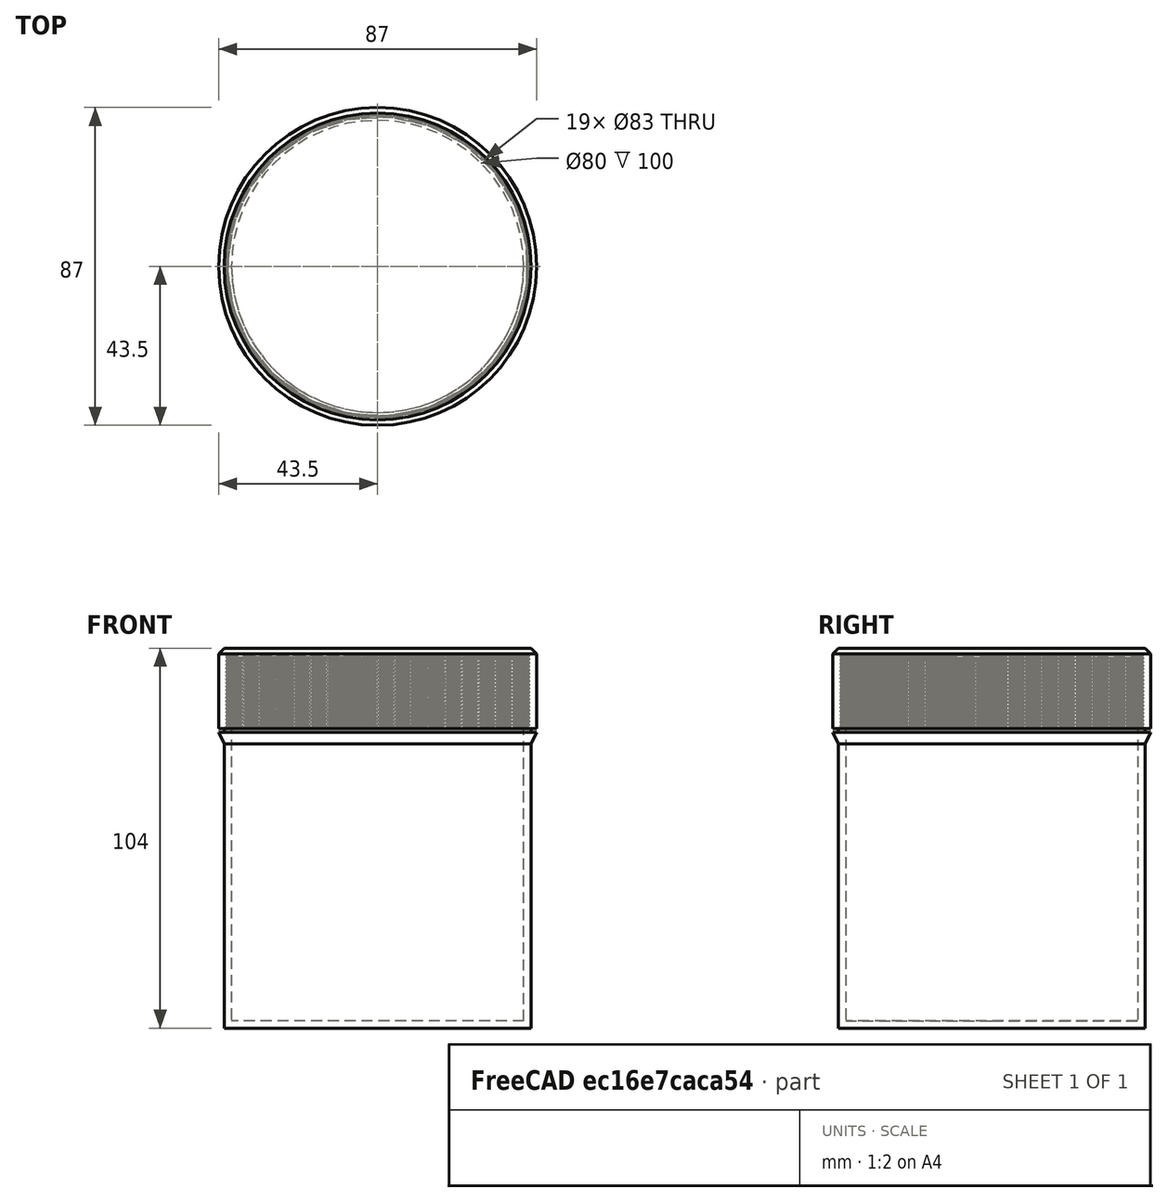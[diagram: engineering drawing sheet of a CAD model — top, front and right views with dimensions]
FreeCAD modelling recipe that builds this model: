
FCSTD DOCUMENT  (FreeCAD 1.0R38641 +678 (Git))
Label: Parametric Screw Top Container
License: All rights reserved
LicenseURL: http://en.wikipedia.org/wiki/All_rights_reserved
objects: Sketcher::SketchObject×9, PartDesign::Pad×2, PartDesign::AdditiveHelix×2, PartDesign::Groove×2, PartDesign::Revolution×2, PartDesign::Body×2, Spreadsheet::Sheet×1, PartDesign::Pocket×1
note: 47 computed .brp shape members not serialized (recipe doc carries the construction recipe); baked Part::Feature solids carry a one-line shape summary decoded from their .brp

FEATURE [Spreadsheet::Sheet] Spreadsheet  label="Parameters"
  cells = A2='Property; B2='Value; D2='Calculated Properties; G2='Some Presets; H2='Stores...; A3='Inner Diameter; B3(innerdiameter)==80 mm; D3='Thread Pitch; E3(threadpitch)==ceil(B5 / 2); G3='19.5 x 77.5; H3='50 US Pennies (1 Roll, $0.50); A4='Inner Height; B4(innerheight)==100 mm; D4='Thread Height; E4(threadheight)==B4 * 0.25 > 20 ? 20 mm : B4 * 0.25; G4='21.75 x 74; H4='40 US Nickels (1 Roll, $2); A5='Wall Thickness; B5(wallthickness)==2 mm; D5='Total Height; E5(totalheight)==B4 + B6; G5='18 x 70; H5='50 US Dimes (1 Roll, $5); A6='Floor Thickness; B6(floorthickness)==2 mm; G6='24.5 x 74; H6='40 US Quarters (1 Roll, $10); A7='Cap Thickness; B7(capthickness)==2 mm; G7='29.5 x 40; H7='Complete KLR650 Valve Shim Set; G8='18.5 x 65.1; H8='One 18650 Cell (Natch); G9='10.5 x 45; H9='One AAA Cell; G10='14.5 x 50.5; H10='One AA Cell; G11='26 x 50; H11='One C Cell; G12='33.5 x 60.25; H12='One D Cell
FEATURE [Sketcher::SketchObject] Sketch  label="Floor Sketch"
  ArcFitTolerance = 0
  AttachmentSupport = -> [XY_Plane]
  FullyConstrained = true
  MakeInternals = false
  MapMode = 5
  expr: Constraints[1] = Spreadsheet.innerdiameter + Spreadsheet.wallthickness * 2
  sketch-geometry (1):
    g0: Circle CenterX=0 CenterY=0 CenterZ=0 NormalX=0 NormalY=0 NormalZ=1 AngleXU=0 Radius=42
  constraints (2):
    c: Coincident(g0,g-1)
    c: Diameter(g0) = 84
FEATURE [Sketcher::SketchObject] Sketch001  label="Walls Sketch"
  ArcFitTolerance = 0
  AttachmentOffset = pos=(0,0,2) rot=(0,0,1;0rad)
  AttachmentSupport = -> [XY_Plane]
  FullyConstrained = true
  MakeInternals = false
  MapMode = 5
  Placement = pos=(0,0,2) rot=(0,0,1;0rad)
  expr: .AttachmentOffset.Base.z = Spreadsheet.floorthickness
  expr: Constraints[1] = Spreadsheet.innerdiameter
  expr: Constraints[3] = Spreadsheet.innerdiameter + Spreadsheet.wallthickness * 2
  sketch-geometry (2):
    g0: Circle CenterX=0 CenterY=0 CenterZ=0 NormalX=0 NormalY=0 NormalZ=1 AngleXU=0 Radius=40
    g1: Circle CenterX=0 CenterY=0 CenterZ=0 NormalX=0 NormalY=0 NormalZ=1 AngleXU=0 Radius=42
  constraints (4):
    c: Coincident(g0,g-1)
    c: Diameter(g0) = 80
    c: Coincident(g1,g0)
    c: Diameter(g1) = 84
FEATURE [PartDesign::Pad] Pad  label="Floor Pad"
  Direction = (0,0,1)
  Length = 2
  Length2 = 10
  Profile = -> Sketch
  ReferenceAxis = -> Sketch [N_Axis]
  Suppressed = false
  Type = 0
  expr: Length = Spreadsheet.floorthickness
FEATURE [PartDesign::Pad] Pad001  label="Walls Pad"
  BaseFeature = -> Pad
  Direction = (0,0,1)
  Length = 100
  Length2 = 10
  Profile = -> Sketch001
  ReferenceAxis = -> Sketch001 [N_Axis]
  Suppressed = false
  Type = 0
  expr: Length = Spreadsheet.innerheight
FEATURE [Sketcher::SketchObject] Sketch002  label="Thinner Sketch"
  ArcFitTolerance = 0
  AttachmentOffset = pos=(0,0,102) rot=(0,0,1;0rad)
  AttachmentSupport = -> [XY_Plane]
  FullyConstrained = true
  MakeInternals = false
  MapMode = 5
  Placement = pos=(0,0,102) rot=(0,0,1;0rad)
  expr: .AttachmentOffset.Base.z = Spreadsheet.totalheight
  expr: Constraints[2] = Spreadsheet.innerdiameter + Spreadsheet.wallthickness * 2
  expr: Constraints[3] = Spreadsheet.innerdiameter + Spreadsheet.wallthickness
  sketch-geometry (2):
    g0: Circle CenterX=0 CenterY=0 CenterZ=0 NormalX=0 NormalY=0 NormalZ=1 AngleXU=0 Radius=42
    g1: Circle CenterX=0 CenterY=0 CenterZ=0 NormalX=0 NormalY=0 NormalZ=1 AngleXU=0 Radius=41
  constraints (4):
    c: Coincident(g0,g-1)
    c: Coincident(g1,g0)
    c: Diameter(g0) = 84
    c: Diameter(g1) = 82
FEATURE [PartDesign::Pocket] Pocket  label="Thinner Cut"
  BaseFeature = -> Pad001
  Direction = (0,0,-1)
  Length = 20
  Length2 = 5
  Profile = -> Sketch002
  ReferenceAxis = -> Sketch002 [N_Axis]
  Suppressed = false
  Type = 0
  expr: Length = Spreadsheet.threadheight
FEATURE [Sketcher::SketchObject] Sketch003  label="Male Thread Tooth Sketch"
  ArcFitTolerance = 0
  AttachmentSupport = -> [XZ_Plane]
  FullyConstrained = true
  MakeInternals = false
  MapMode = 5
  Placement = pos=(0,0,0) rot=(1,0,0;1.5708rad)
  expr: Constraints[6] = Spreadsheet.threadpitch - 0.01 mm
  expr: Constraints[7] = Spreadsheet.totalheight
  expr: Constraints[8] = (Spreadsheet.innerdiameter + Spreadsheet.wallthickness) * 0.5 - 0.01 mm
  sketch-geometry (3):
    g0: LineSegment StartX=-40.99 StartY=102.99 StartZ=0 EndX=-41.485 EndY=102.495 EndZ=0
    g1: LineSegment StartX=-41.485 StartY=102.495 StartZ=0 EndX=-40.99 EndY=102 EndZ=0
    g2: LineSegment StartX=-40.99 StartY=102 StartZ=0 EndX=-40.99 EndY=102.99 EndZ=0
  constraints (9):
    c: Coincident(g1,g0)
    c: Coincident(g2,g1)
    c: Coincident(g2,g0)
    c: Vertical(g2)
    c: Equal(g0,g1)
    c: Angle(g1,g0) = 1.5708
    c: DistanceY(g2,g2) = 0.99
    c: DistanceY(g-1,g1) = 102
    c: DistanceX(g1,g-1) = 40.99
FEATURE [PartDesign::AdditiveHelix] AdditiveHelix  label="Male Thread"
  Angle = 0
  Axis = (0,2e-16,1)
  Base = (0,0,0)
  BaseFeature = -> Pocket
  Growth = 0
  HasBeenEdited = true
  Height = 21
  LeftHanded = false
  Mode = 0
  Outside = false
  Pitch = 1
  Profile = -> Sketch003
  ReferenceAxis = -> Sketch003 [V_Axis]
  Reversed = true
  Suppressed = false
  Tolerance = 0.1
  Turns = 21
  expr: Height = Spreadsheet.threadheight + Spreadsheet.threadpitch
  expr: Pitch = Spreadsheet.threadpitch
FEATURE [Sketcher::SketchObject] Sketch004  label="Male Nosifier"
  ArcFitTolerance = 0
  AttachmentSupport = -> [XZ_Plane]
  FullyConstrained = true
  MakeInternals = false
  MapMode = 5
  Placement = pos=(0,0,0) rot=(1,0,0;1.5708rad)
  expr: Constraints[10] = Spreadsheet.wallthickness
  expr: Constraints[11] = Spreadsheet.threadpitch * 2
  expr: Constraints[12] = Spreadsheet.wallthickness * 2
  expr: Constraints[13] = Spreadsheet.totalheight
  expr: Constraints[14] = Spreadsheet.innerdiameter * 0.5
  sketch-geometry (5):
    g0: LineSegment StartX=-38 StartY=102 StartZ=0 EndX=-40 EndY=102 EndZ=0
    g1: LineSegment StartX=-40 StartY=102 StartZ=0 EndX=-42 EndY=100.845 EndZ=0
    g2: LineSegment StartX=-42 StartY=100.845 StartZ=0 EndX=-42 EndY=104 EndZ=0
    g3: LineSegment StartX=-42 StartY=104 StartZ=0 EndX=-38 EndY=104 EndZ=0
    g4: LineSegment StartX=-38 StartY=104 StartZ=0 EndX=-38 EndY=102 EndZ=0
  constraints (15):
    c: Horizontal(g0)
    c: Coincident(g0,g1)
    c: Coincident(g1,g2)
    c: Vertical(g2)
    c: Coincident(g2,g3)
    c: Horizontal(g3)
    c: Coincident(g3,g4)
    c: Coincident(g4,g0)
    c: Vertical(g4)
    c: Angle(g1,g2) = 1.0472
    c: DistanceX(g1,g0) = 2
    c: DistanceY(g4,g4) = 2
    c: DistanceX(g3,g3) = 4
    c: DistanceY(g-1,g0) = 102
    c: DistanceX(g0,g-1) = 40
FEATURE [PartDesign::Groove] Groove  label="Male Thread Nosification"
  Angle = 360
  Angle2 = 60
  Axis = (0,2e-16,1)
  Base = (0,0,0)
  BaseFeature = -> AdditiveHelix
  Profile = -> Sketch004
  ReferenceAxis = -> Sketch004 [V_Axis]
  Reversed = true
  Suppressed = false
  Type = 0
FEATURE [Sketcher::SketchObject] Sketch005  label="Cap Profile Sketch"
  ArcFitTolerance = 0
  AttachmentSupport = -> [XZ_Plane001]
  FullyConstrained = true
  MakeInternals = false
  MapMode = 5
  Placement = pos=(0,0,0) rot=(1,0,0;1.5708rad)
  expr: Constraints[14] = Spreadsheet.innerdiameter * 0.5 + Spreadsheet.wallthickness * 0.5 + Spreadsheet.threadpitch * 0.5
  expr: Constraints[15] = Spreadsheet.wallthickness
  expr: Constraints[17] = Spreadsheet.capthickness
  expr: Constraints[18] = Spreadsheet.threadheight
  expr: Constraints[19] = Spreadsheet.wallthickness * 0.75
  expr: Constraints[20] = Spreadsheet.totalheight
  sketch-geometry (7):
    g0: LineSegment StartX=0 StartY=102 StartZ=0 EndX=-41.5 EndY=102 EndZ=0
    g1: LineSegment StartX=-41.5 StartY=102 StartZ=0 EndX=-41.5 EndY=82 EndZ=0
    g2: LineSegment StartX=-41.5 StartY=82 StartZ=0 EndX=-43.5 EndY=82 EndZ=0
    g3: LineSegment StartX=-43.5 StartY=82 StartZ=0 EndX=-43.5 EndY=102.5 EndZ=0
    g4: LineSegment StartX=-43.5 StartY=102.5 StartZ=0 EndX=-42 EndY=104 EndZ=0
    g5: LineSegment StartX=-42 StartY=104 StartZ=0 EndX=0 EndY=104 EndZ=0
    g6: LineSegment StartX=0 StartY=104 StartZ=0 EndX=0 EndY=102 EndZ=0
  constraints (21):
    c: PointOnObject(g0,g-2)
    c: Horizontal(g0)
    c: Coincident(g0,g1)
    c: Vertical(g1)
    c: Coincident(g1,g2)
    c: Horizontal(g2)
    c: Coincident(g2,g3)
    c: Vertical(g3)
    c: Coincident(g3,g4)
    c: Coincident(g4,g5)
    c: PointOnObject(g5,g-2)
    c: Horizontal(g5)
    c: Coincident(g5,g6)
    c: Coincident(g6,g0)
    c: DistanceX(g0,g0) = 41.5
    c: DistanceX(g2,g2) = 2
    c: Angle(g3,g4) = 2.35619
    c: DistanceY(g6,g6) = 2
    c: DistanceY(g1,g1) = 20
    c: DistanceX(g3,g4) = 1.5
    c: DistanceY(g-1,g0) = 102
FEATURE [Sketcher::SketchObject] Sketch006  label="Female Thread Tooth"
  ArcFitTolerance = 0
  AttachmentSupport = -> [XZ_Plane001]
  FullyConstrained = true
  MakeInternals = false
  MapMode = 5
  Placement = pos=(0,0,0) rot=(1,0,0;1.5708rad)
  expr: Constraints[4] = Spreadsheet.threadpitch - 0.01 mm
  expr: Constraints[7] = Spreadsheet.innerdiameter * 0.5 + Spreadsheet.wallthickness * 0.5 + Spreadsheet.threadpitch * 0.5 + 0.1 mm
  expr: Constraints[8] = Spreadsheet.totalheight + Spreadsheet.threadpitch * 0.5
  sketch-geometry (3):
    g0: LineSegment StartX=-41.6 StartY=101.51 StartZ=0 EndX=-41.6 EndY=102.5 EndZ=0
    g1: LineSegment StartX=-41.6 StartY=102.5 StartZ=0 EndX=-41.105 EndY=102.005 EndZ=0
    g2: LineSegment StartX=-41.105 StartY=102.005 StartZ=0 EndX=-41.6 EndY=101.51 EndZ=0
  constraints (9):
    c: Vertical(g0)
    c: Coincident(g0,g1)
    c: Coincident(g1,g2)
    c: Coincident(g2,g0)
    c: DistanceY(g0,g0) = 0.99
    c: Angle(g1,g2) = 1.5708
    c: Equal(g1,g2)
    c: DistanceX(g0,g-1) = 41.6
    c: DistanceY(g-1,g0) = 102.5
FEATURE [PartDesign::Revolution] Revolution  label="Cap Revolve"
  Angle = 360
  Angle2 = 60
  Axis = (0,2e-16,1)
  Base = (0,0,0)
  Placement = pos=(0,0,0) rot=(1,0,0;1.5708rad)
  Profile = -> Sketch005
  ReferenceAxis = -> Sketch005 [V_Axis]
  Suppressed = false
  Type = 0
FEATURE [PartDesign::AdditiveHelix] AdditiveHelix001  label="Female Thread"
  Angle = 0
  Axis = (0,2e-16,1)
  Base = (0,0,0)
  BaseFeature = -> Revolution
  Growth = 0
  HasBeenEdited = true
  Height = 20
  LeftHanded = false
  Mode = 0
  Outside = false
  Pitch = 1
  Placement = pos=(0,0,0) rot=(1,0,0;1.5708rad)
  Profile = -> Sketch006
  ReferenceAxis = -> Sketch006 [V_Axis]
  Reversed = true
  Suppressed = false
  Tolerance = 0.1
  Turns = 20
  expr: Height = Spreadsheet.threadheight
  expr: Pitch = Spreadsheet.threadpitch
FEATURE [Sketcher::SketchObject] Sketch007  label="Female Nosifier Sketch"
  ArcFitTolerance = 0
  AttachmentSupport = -> [XZ_Plane001]
  FullyConstrained = true
  MakeInternals = false
  MapMode = 5
  Placement = pos=(0,0,0) rot=(1,0,0;1.5708rad)
  expr: Constraints[10] = Spreadsheet.threadpitch * 3
  expr: Constraints[11] = Spreadsheet.totalheight - Spreadsheet.threadheight + 0.01 mm
  expr: Constraints[9] = Spreadsheet.innerdiameter
  sketch-geometry (4):
    g0: LineSegment StartX=0 StartY=82.01 StartZ=0 EndX=-80 EndY=82.01 EndZ=0
    g1: LineSegment StartX=-80 StartY=82.01 StartZ=0 EndX=-80 EndY=79.01 EndZ=0
    g2: LineSegment StartX=-80 StartY=79.01 StartZ=0 EndX=0 EndY=79.01 EndZ=0
    g3: LineSegment StartX=0 StartY=79.01 StartZ=0 EndX=0 EndY=82.01 EndZ=0
  constraints (12):
    c: Coincident(g0,g1)
    c: Coincident(g1,g2)
    c: Coincident(g2,g3)
    c: Coincident(g3,g0)
    c: Horizontal(g0)
    c: Horizontal(g2)
    c: Vertical(g1)
    c: Vertical(g3)
    c: PointOnObject(g0,g-2)
    c: DistanceX(g0,g0) = 80
    c: DistanceY(g3,g3) = 3
    c: DistanceY(g-1,g0) = 82.01
FEATURE [PartDesign::Groove] Groove001  label="Female Thread Nosification"
  Angle = 360
  Angle2 = 60
  Axis = (0,2e-16,1)
  Base = (0,0,0)
  BaseFeature = -> AdditiveHelix001
  Placement = pos=(0,0,0) rot=(1,0,0;1.5708rad)
  Profile = -> Sketch007
  ReferenceAxis = -> Sketch007 [V_Axis]
  Reversed = true
  Suppressed = false
  Type = 0
FEATURE [PartDesign::Body] Body001  label="Cap"
  AllowCompound = false
  Group = -> [Sketch005,Sketch006,Revolution,AdditiveHelix001,Sketch007,Groove001]
  Origin = -> Origin001
  Tip = -> Groove001
FEATURE [Sketcher::SketchObject] Sketch008  label="Endstop Ring Sketch"
  ArcFitTolerance = 0
  AttachmentSupport = -> [XZ_Plane]
  FullyConstrained = true
  MakeInternals = false
  MapMode = 5
  Placement = pos=(0,0,0) rot=(1,0,0;1.5708rad)
  expr: Constraints[6] = Spreadsheet.wallthickness * 0.75
  expr: Constraints[7] = (Spreadsheet.innerdiameter + Spreadsheet.wallthickness * 2) * 0.5
  expr: Constraints[8] = Spreadsheet.totalheight - Spreadsheet.threadheight - Spreadsheet.threadpitch
  sketch-geometry (3):
    g0: LineSegment StartX=-42 StartY=77.7832 StartZ=0 EndX=-42 EndY=81 EndZ=0
    g1: LineSegment StartX=-42 StartY=81 StartZ=0 EndX=-43.5 EndY=81 EndZ=0
    g2: LineSegment StartX=-43.5 StartY=81 StartZ=0 EndX=-42 EndY=77.7832 EndZ=0
  constraints (9):
    c: Vertical(g0)
    c: Coincident(g0,g1)
    c: Horizontal(g1)
    c: Coincident(g1,g2)
    c: Coincident(g2,g0)
    c: Angle(g0,g2) = 0.436332
    c: DistanceX(g1,g1) = 1.5
    c: DistanceX(g0,g-1) = 42
    c: DistanceY(g-1,g0) = 81
FEATURE [PartDesign::Revolution] Revolution001  label="Endstop Ring"
  Angle = 360
  Angle2 = 60
  Axis = (0,2e-16,1)
  Base = (0,0,0)
  BaseFeature = -> Groove
  Profile = -> Sketch008
  ReferenceAxis = -> Sketch008 [V_Axis]
  Suppressed = false
  Type = 0
FEATURE [PartDesign::Body] Body  label="Base"
  AllowCompound = false
  Group = -> [Sketch,Sketch001,Pad,Pad001,Sketch002,Pocket,Sketch003,AdditiveHelix,Sketch004,Groove,Sketch008,Revolution001]
  Origin = -> Origin
  Tip = -> Revolution001
